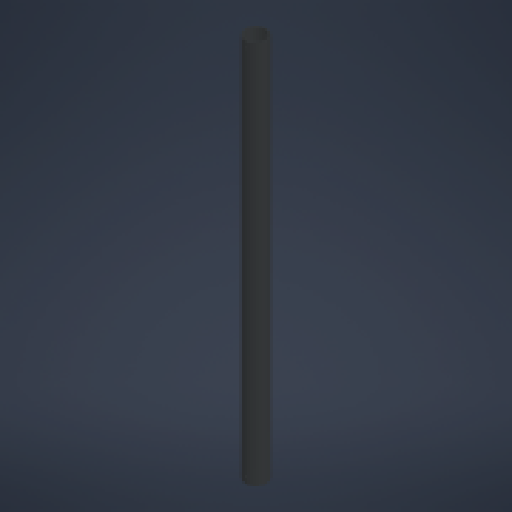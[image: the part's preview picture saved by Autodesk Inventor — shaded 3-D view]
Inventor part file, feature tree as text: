
AUTODESK INVENTOR PART (.ipt)
format: ipt  version: 2024 (Build 280153000, 153)  size: 125,952 bytes
history: native  units: in
note: dims shown in document units (in); Inventor stores cm internally (conversion verified against a paired STEP export)
features: mirror x1
ambient origin geometry x8: Origin, YZ Plane, XZ Plane, XY Plane, X Axis, Y Axis, Z Axis, Center Point
bodies: Solid1 (feature_tree)
feature tree (1):
  mirror  "Mirror1"
